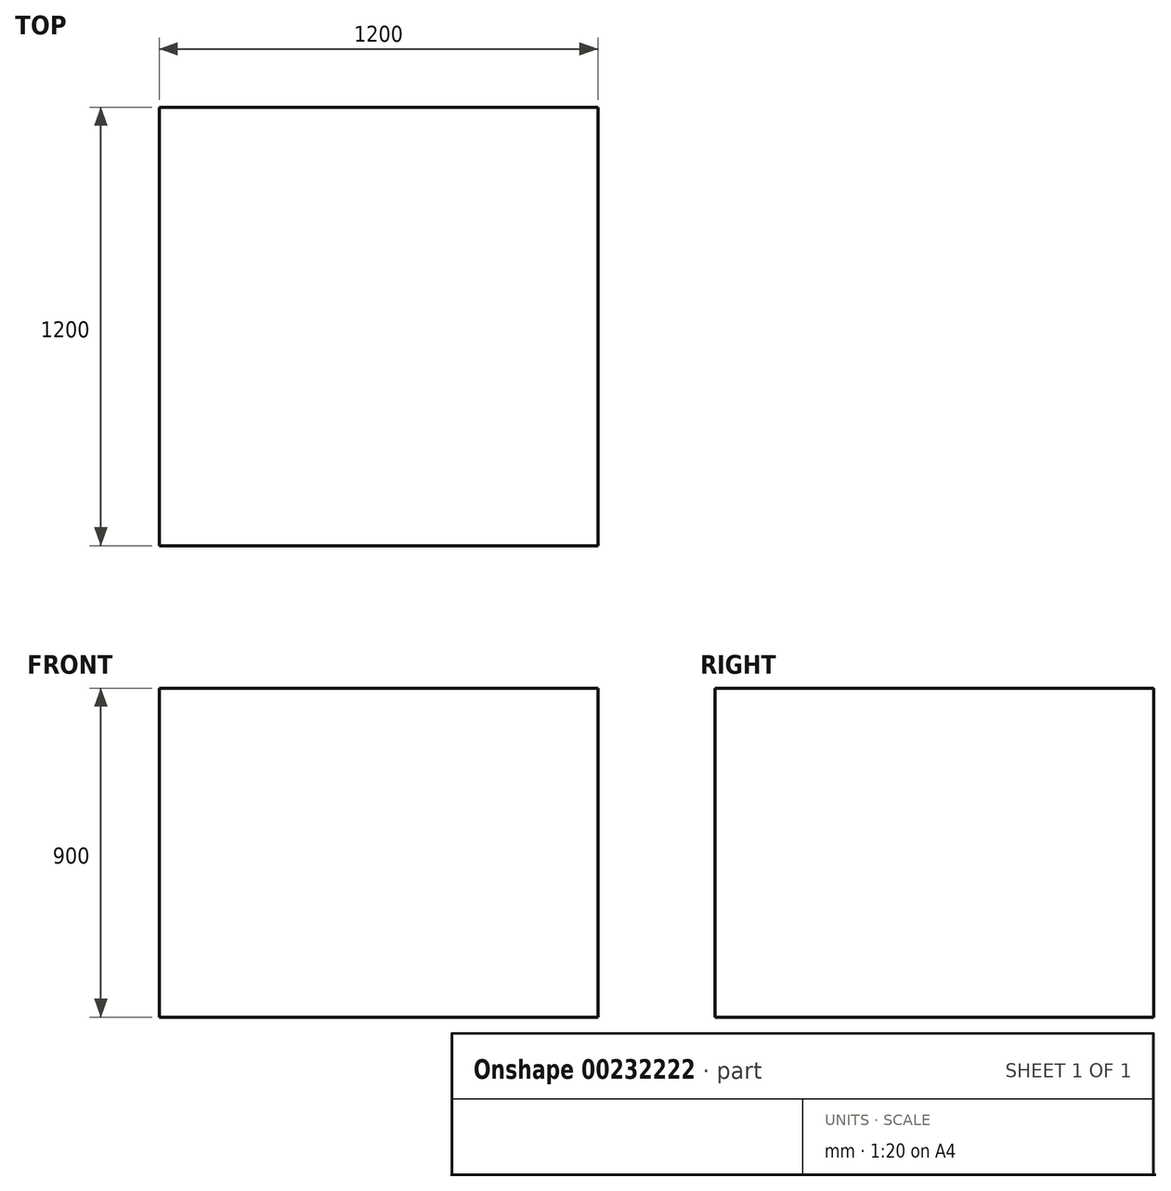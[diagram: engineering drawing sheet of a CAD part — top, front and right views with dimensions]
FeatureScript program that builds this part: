
annotation { "Feature Type Name" : "Feature", "Feature Type Description" : "" }
export const myFeature = defineFeature(function(context is Context, id is Id, definition is map)
    precondition{}
    {
        {
            var Q0;
            Q0=qCreatedBy(makeId("Top.planeOp"),FACE);
            var sketch = newSketch(context, id + "F0", { "sketchPlane" : qUnion([Q0])});
            skLineSegment(sketch, "E0.bottom", {"start": v(600, 600) * mm, "end": v(-600, 600) * mm});
            skLineSegment(sketch, "E0.top", {"start": v(600, -600) * mm, "end": v(-600, -600) * mm});
            skLineSegment(sketch, "E0.left", {"start": v(600, 600) * mm, "end": v(600, -600) * mm});
            skLineSegment(sketch, "E0.right", {"start": v(-600, 600) * mm, "end": v(-600, -600) * mm});
            skPoint(sketch, "E0.middle", {"position": v(0, 0) * mm});
            skSolve(sketch);
        }
        {
            var Q0;
            Q0 = qSketchRegion(id + "F0", true);
            extrude(context, id + "F1", {"entities" : qUnion([Q0]), "flatOperationType" : FlatOperationType.REMOVE, "offsetDistance" : 25 * mm, "depth" : 900 * mm, "domain" : OperationDomain.MODEL, "symmetric" : true});
        }
    });
